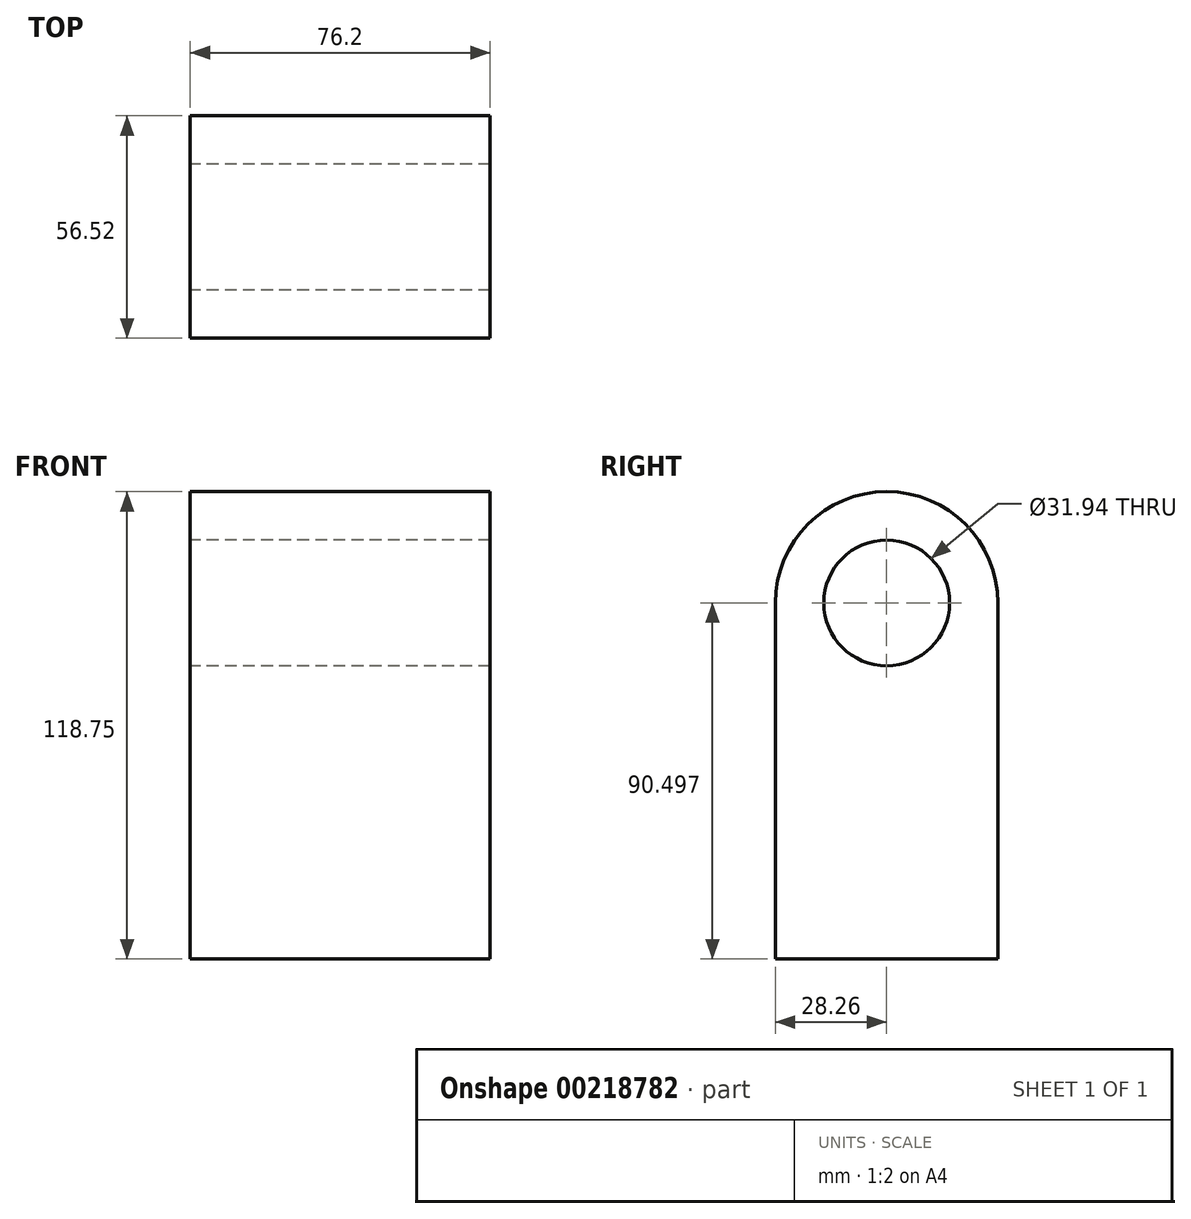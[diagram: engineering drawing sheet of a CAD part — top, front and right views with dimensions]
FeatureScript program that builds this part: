
annotation { "Feature Type Name" : "Feature", "Feature Type Description" : "" }
export const myFeature = defineFeature(function(context is Context, id is Id, definition is map)
    precondition{}
    {
        {
            var Q0;
            Q0=qCreatedBy(makeId("Right.planeOp"),FACE);
            var sketch = newSketch(context, id + "F0", { "sketchPlane" : qUnion([Q0])});
            skLineSegment(sketch, "E0.top", {"start": v(-28.26, -45.25) * mm, "end": v(28.26, -45.25) * mm});
            skLineSegment(sketch, "E0.left", {"start": v(-28.26, 45.25) * mm, "end": v(-28.26, -45.25) * mm});
            skLineSegment(sketch, "E0.right", {"start": v(28.26, 45.25) * mm, "end": v(28.26, -45.25) * mm});
            skPoint(sketch, "E0.middle", {"position": v(0, 0) * mm});
            skArc(sketch, "E1", {"start": v(28.26, 45.25) * mm, "mid": v(0, 73.5) * mm, "end": v(-28.26, 45.25) * mm});
            skCircle(sketch, "E2", {"center": v(0, 45.25) * mm, "radius": 15.97 * mm});
            skSolve(sketch);
        }
        {
            var Q0;
            Q0=makeQuery(id+"F0.imprint","IMPRINT",FACE,{"disambiguationData":[TD([[makeQuery(id+"F0.imprint","IMPRINT",EDGE,{"derivedFrom":sQuery(id+"F0.wireOp",EDGE,"E0.top")}),1.0]])]});
            extrude(context, id + "F1", {"entities" : qUnion([Q0]), "depth" : 76.2 * mm});
        }
    });
